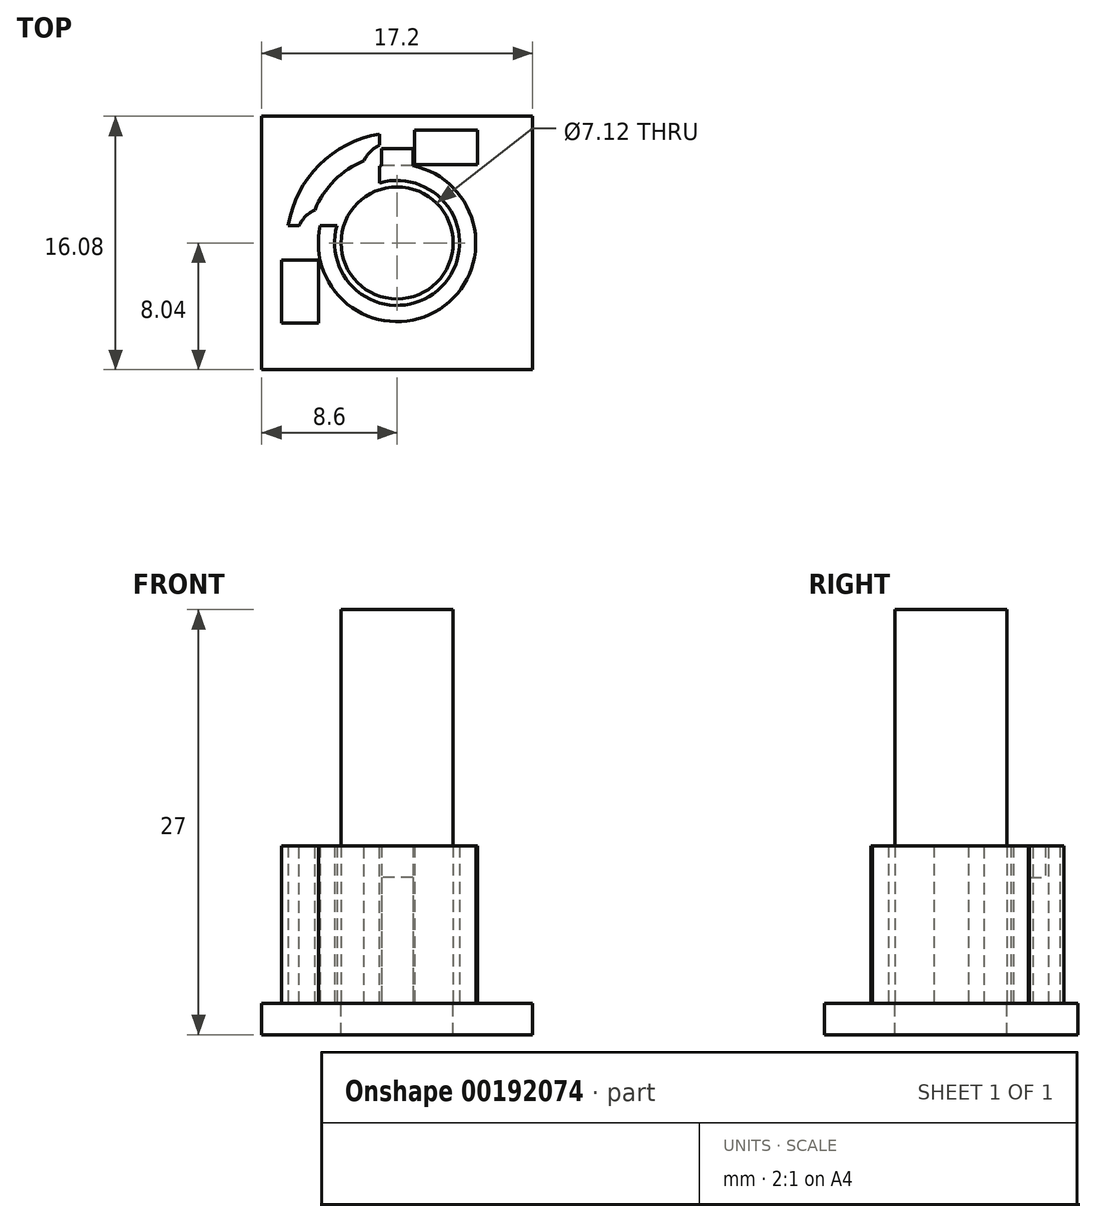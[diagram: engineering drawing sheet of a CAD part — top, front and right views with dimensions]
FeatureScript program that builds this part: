
annotation { "Feature Type Name" : "Feature", "Feature Type Description" : "" }
export const myFeature = defineFeature(function(context is Context, id is Id, definition is map)
    precondition{}
    {
        {
            var Q0;
            Q0=qCreatedBy(makeId("Top.planeOp"),FACE);
            var sketch = newSketch(context, id + "F0", { "sketchPlane" : qUnion([Q0])});
            skCircle(sketch, "E0", {"center": v(0, 0) * mm, "radius": 5 * mm});
            skLineSegment(sketch, "E1", {"start": v(-3.5, 6.59) * mm, "end": v(3.5, 6.59) * mm, "construction": true});
            skLineSegment(sketch, "E2", {"start": v(3.5, 6.59) * mm, "end": v(0, 10.09) * mm, "construction": true});
            skLineSegment(sketch, "E3", {"start": v(0, 10.09) * mm, "end": v(-3.5, 6.59) * mm, "construction": true});
            skLineSegment(sketch, "E4", {"start": v(0, 5.96) * mm, "end": v(0, 19.7) * mm, "construction": true});
            skLineSegment(sketch, "E5.top", {"start": v(1, 6) * mm, "end": v(-1, 6) * mm});
            skLineSegment(sketch, "E5.left", {"start": v(1, 4.9) * mm, "end": v(1, 6) * mm});
            skLineSegment(sketch, "E5.right", {"start": v(-1, 4.9) * mm, "end": v(-1, 6) * mm});
            skPoint(sketch, "E5.middle", {"position": v(0, 5) * mm});
            skSolve(sketch);
        }
        {
            var Q0;
            Q0 = qSketchRegion(id + "F0", true);
            extrude(context, id + "F1", {"entities" : qUnion([Q0]), "depth" : 10 * mm});
        }
        {
            var Q0;
            Q0=qCreatedBy(makeId("Top.planeOp"),FACE);
            var sketch = newSketch(context, id + "F2", { "sketchPlane" : qUnion([Q0])});
            skArc(sketch, "E6", {"start": v(-1.1, 5.13) * mm, "mid": v(-3.71, 3.71) * mm, "end": v(-5.13, 1.1) * mm});
            skArc(sketch, "E7", {"start": v(-1.1, 6.91) * mm, "mid": v(-4.95, 4.95) * mm, "end": v(-6.91, 1.1) * mm});
            skPoint(sketch, "E8", {"position": v(-5.25, 0) * mm});
            skLineSegment(sketch, "E9", {"start": v(0, 0) * mm, "end": v(-10.53, 0) * mm, "construction": true});
            skLineSegment(sketch, "E10", {"start": v(0, 0) * mm, "end": v(-6.32, 6.32) * mm, "construction": true});
            skLineSegment(sketch, "E11", {"start": v(0, 0) * mm, "end": v(0, 8.76) * mm, "construction": true});
            skPoint(sketch, "E12", {"position": v(0, 7) * mm});
            skPoint(sketch, "E13", {"position": v(0, 5.25) * mm});
            skLineSegment(sketch, "E14", {"start": v(-1.1, 5.13) * mm, "end": v(-1.1, 6.91) * mm});
            skLineSegment(sketch, "E15", {"start": v(1.1, 6.91) * mm, "end": v(1.1, 5.13) * mm, "construction": true});
            skLineSegment(sketch, "E16", {"start": v(-6.91, 1.1) * mm, "end": v(-5.13, 1.1) * mm});
            skLineSegment(sketch, "E17", {"start": v(-6.91, -1.1) * mm, "end": v(-5.13, -1.1) * mm, "construction": true});
            skArc(sketch, "E18.trimOffspring", {"start": v(-6.91, -1.1) * mm, "mid": v(4.95, -4.95) * mm, "end": v(1.1, 6.91) * mm, "construction": true});
            skArc(sketch, "E19.trimOffspring", {"start": v(-5.13, -1.1) * mm, "mid": v(3.71, -3.71) * mm, "end": v(1.1, 5.13) * mm, "construction": true});
            skLineSegment(sketch, "E20.bottom", {"start": v(1.1, 7.16) * mm, "end": v(5.1, 7.16) * mm});
            skLineSegment(sketch, "E20.top", {"start": v(1.1, 4.98) * mm, "end": v(5.1, 4.98) * mm});
            skLineSegment(sketch, "E20.left", {"start": v(1.1, 7.16) * mm, "end": v(1.1, 4.98) * mm});
            skLineSegment(sketch, "E20.right", {"start": v(5.1, 7.16) * mm, "end": v(5.1, 4.98) * mm});
            skLineSegment(sketch, "E21.bottom", {"start": v(-7.35, -1.1) * mm, "end": v(-4.99, -1.1) * mm});
            skLineSegment(sketch, "E21.top", {"start": v(-7.35, -5.1) * mm, "end": v(-4.99, -5.1) * mm});
            skLineSegment(sketch, "E21.left", {"start": v(-7.35, -1.1) * mm, "end": v(-7.35, -5.1) * mm});
            skLineSegment(sketch, "E21.right", {"start": v(-4.99, -1.1) * mm, "end": v(-4.99, -5.1) * mm});
            skSolve(sketch);
        }
        {
            var Q0;
            {var subQ0=sQuery(id+"F2.wireOp",EDGE,"E14");Q0=makeQuery(id+"F2.imprint","IMPRINT",FACE,{"disambiguationData":[TD([[makeQuery(id+"F2.imprint","IMPRINT",EDGE,{"derivedFrom":subQ0}),1.0]])]});}
            var Q1;
            {var subQ0=sQuery(id+"F2.wireOp",EDGE,"E15");Q1=makeQuery(id+"F2.imprint","IMPRINT",FACE,{"disambiguationData":[TD([[makeQuery(id+"F2.imprint","IMPRINT",EDGE,{"derivedFrom":subQ0}),1.0]])]});}
            var Q2;
            Q2=makeQuery(id+"F2.imprint","IMPRINT",FACE,{"disambiguationData":[TD([[makeQuery(id+"F2.imprint","IMPRINT",EDGE,{"derivedFrom":sQuery(id+"F2.wireOp",EDGE,"E20.bottom")}),-1.0]])]});
            var Q3;
            Q3=makeQuery(id+"F2.imprint","IMPRINT",FACE,{"disambiguationData":[TD([[makeQuery(id+"F2.imprint","IMPRINT",EDGE,{"derivedFrom":sQuery(id+"F2.wireOp",EDGE,"E21.bottom")}),-1.0]])]});
            extrude(context, id + "F3", {"entities" : qUnion([Q0, Q1, Q2, Q3]), "depth" : 10 * mm});
        }
        {
            var Q0;
            Q0=makeQuery(id+"F1.opExtrude","CAP_FACE",FACE,{"disambiguationData":[OSD([sQuery(id+"F0.wireOp",EDGE,"E0"),sQuery(id+"F0.wireOp",EDGE,"E2"),sQuery(id+"F0.wireOp",EDGE,"E3")])],"isStart":true});
            var sketch = newSketch(context, id + "F4", { "sketchPlane" : qUnion([Q0])});
            skCircle(sketch, "E22", {"center": v(0, 0) * mm, "radius": 3.97 * mm});
            skSolve(sketch);
        }
        {
            var Q0;
            Q0 = qSketchRegion(id + "F4", true);
            extrude(context, id + "F5", {"entities" : qUnion([Q0]), "operationType" : NewBodyOperationType.REMOVE, "oppositeDirection" : true, "depth" : 25 * mm});
        }
        {
            var Q0;
            Q0=qCreatedBy(makeId("Top.planeOp"),FACE);
            var sketch = newSketch(context, id + "F6", { "sketchPlane" : qUnion([Q0])});
            skLineSegment(sketch, "E23.bottom", {"start": v(8.6, -8.04) * mm, "end": v(-8.6, -8.04) * mm});
            skLineSegment(sketch, "E23.top", {"start": v(8.6, 8.04) * mm, "end": v(-8.6, 8.04) * mm});
            skLineSegment(sketch, "E23.left", {"start": v(8.6, -8.04) * mm, "end": v(8.6, 8.04) * mm});
            skLineSegment(sketch, "E23.right", {"start": v(-8.6, -8.04) * mm, "end": v(-8.6, 8.04) * mm});
            skPoint(sketch, "E23.middle", {"position": v(0, 0) * mm});
            skSolve(sketch);
        }
        {
            var Q0;
            Q0 = qSketchRegion(id + "F6", true);
            extrude(context, id + "F7", {"entities" : qUnion([Q0]), "operationType" : NewBodyOperationType.ADD, "oppositeDirection" : true, "depth" : 2 * mm});
        }
        {
            var Q0;
            Q0=makeQuery(id+"F7.opExtrude","CAP_FACE",FACE,{"disambiguationData":[OSD([sQuery(id+"F6.wireOp",EDGE,"E23.bottom"),sQuery(id+"F6.wireOp",EDGE,"E23.top"),sQuery(id+"F6.wireOp",EDGE,"E23.left"),sQuery(id+"F6.wireOp",EDGE,"E23.right")])],"isStart":true});
            var sketch = newSketch(context, id + "F8", { "sketchPlane" : qUnion([Q0])});
            skCircle(sketch, "E24", {"center": v(0, 0) * mm, "radius": 3.56 * mm});
            skSolve(sketch);
        }
        {
            var Q0;
            Q0 = qSketchRegion(id + "F8", true);
            extrude(context, id + "F9", {"entities" : qUnion([Q0]), "operationType" : NewBodyOperationType.REMOVE, "oppositeDirection" : true, "depth" : 15 * mm});
        }
        {
            var Q0;
            Q0=makeQuery(id+"F3.opExtrude","CAP_FACE",FACE,{"disambiguationData":[OSD([sQuery(id+"F2.wireOp",EDGE,"E6"),sQuery(id+"F2.wireOp",EDGE,"E7"),sQuery(id+"F2.wireOp",EDGE,"E14"),sQuery(id+"F2.wireOp",EDGE,"E16")])],"isStart":false});
            var sketch = newSketch(context, id + "F10", { "sketchPlane" : qUnion([Q0])});
            skPoint(sketch, "E25", {"position": v(-1.1, 5.51) * mm});
            skPoint(sketch, "E26", {"position": v(-5.51, 1.1) * mm});
            skArc(sketch, "E27", {"start": v(-1.1, 5.51) * mm, "mid": v(-3.98, 3.98) * mm, "end": v(-5.51, 1.1) * mm});
            skLineSegment(sketch, "E28", {"start": v(-5.51, 1.1) * mm, "end": v(-1.1, 1.1) * mm});
            skLineSegment(sketch, "E29", {"start": v(-1.1, 1.1) * mm, "end": v(-1.1, 5.51) * mm});
            skLineSegment(sketch, "E30", {"start": v(-1.1, 6.21) * mm, "end": v(-1.1, 5.51) * mm});
            skLineSegment(sketch, "E31", {"start": v(-6.21, 1.1) * mm, "end": v(-5.51, 1.1) * mm});
            skPoint(sketch, "E32", {"position": v(-1.8, 5.51) * mm});
            skArc(sketch, "E33", {"start": v(-5.21, 2.1) * mm, "mid": v(-5.8, 1.7) * mm, "end": v(-6.21, 1.1) * mm});
            skArc(sketch, "E34", {"start": v(-1.1, 6.21) * mm, "mid": v(-1.7, 5.8) * mm, "end": v(-2.1, 5.21) * mm});
            skSolve(sketch);
        }
        {
            var Q0;
            Q0 = qSketchRegion(id + "F10", true);
            extrude(context, id + "F11", {"entities" : qUnion([Q0]), "operationType" : NewBodyOperationType.REMOVE, "oppositeDirection" : true, "depth" : 10 * mm});
        }
        {
            var Q0;
            Q0=makeQuery(id+"F1.opExtrude","SWEPT_FACE",FACE,{"disambiguationData":[OSD([sQuery(id+"F0.wireOp",EDGE,"E5.top")])]});
            var sketch = newSketch(context, id + "F12", { "sketchPlane" : qUnion([Q0])});
            skLineSegment(sketch, "E35.bottom", {"start": v(-1, 8) * mm, "end": v(1, 8) * mm});
            skLineSegment(sketch, "E35.top", {"start": v(-1, 0) * mm, "end": v(1, 0) * mm});
            skLineSegment(sketch, "E35.left", {"start": v(-1, 8) * mm, "end": v(-1, 0) * mm});
            skLineSegment(sketch, "E35.right", {"start": v(1, 8) * mm, "end": v(1, 0) * mm});
            skSolve(sketch);
        }
        {
            var Q0;
            Q0 = qSketchRegion(id + "F12", true);
            extrude(context, id + "F13", {"entities" : qUnion([Q0]), "operationType" : NewBodyOperationType.REMOVE, "oppositeDirection" : true, "depth" : 1.1 * mm});
        }
        {
            var Q0;
            Q0=makeQuery(id+"F8.imprint","IMPRINT",FACE,{"disambiguationData":[TD([[makeQuery(id+"F8.imprint","IMPRINT",EDGE,{"derivedFrom":sQuery(id+"F8.wireOp",EDGE,"E24")}),1.0]])]});
            extrude(context, id + "F14", {"entities" : qUnion([Q0]), "depth" : 25 * mm});
        }
    });
